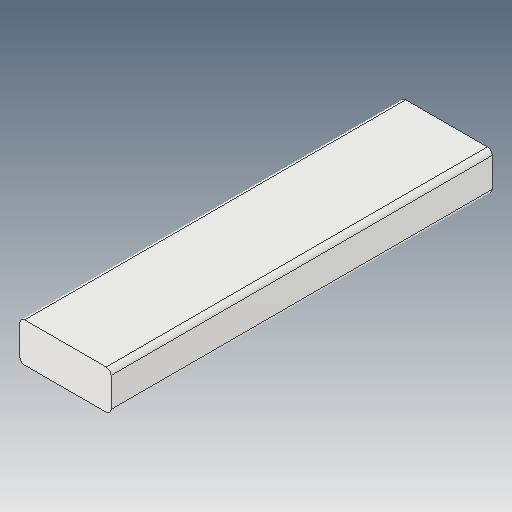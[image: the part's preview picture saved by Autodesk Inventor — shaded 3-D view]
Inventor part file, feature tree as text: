
AUTODESK INVENTOR PART (.ipt)
format: ipt  version: 2023.5 (Build 275446000, 446)  size: 87,552 bytes
history: native  units: in
note: dims shown in document units (in); Inventor stores cm internally (conversion verified against a paired STEP export)
features: fillet x1
ambient origin geometry x8: Origin, YZ Plane, XZ Plane, XY Plane, X Axis, Y Axis, Z Axis, Center Point
bodies: Solid1 (feature_tree)
feature tree (1):
  fillet  "Fillet1"  [1 undecoded]
note: 1 required parameter value undecoded (feature->parameter linkage not recoverable at this tier; creation-order binding heuristic only, values carry confidence <= 0.55)
